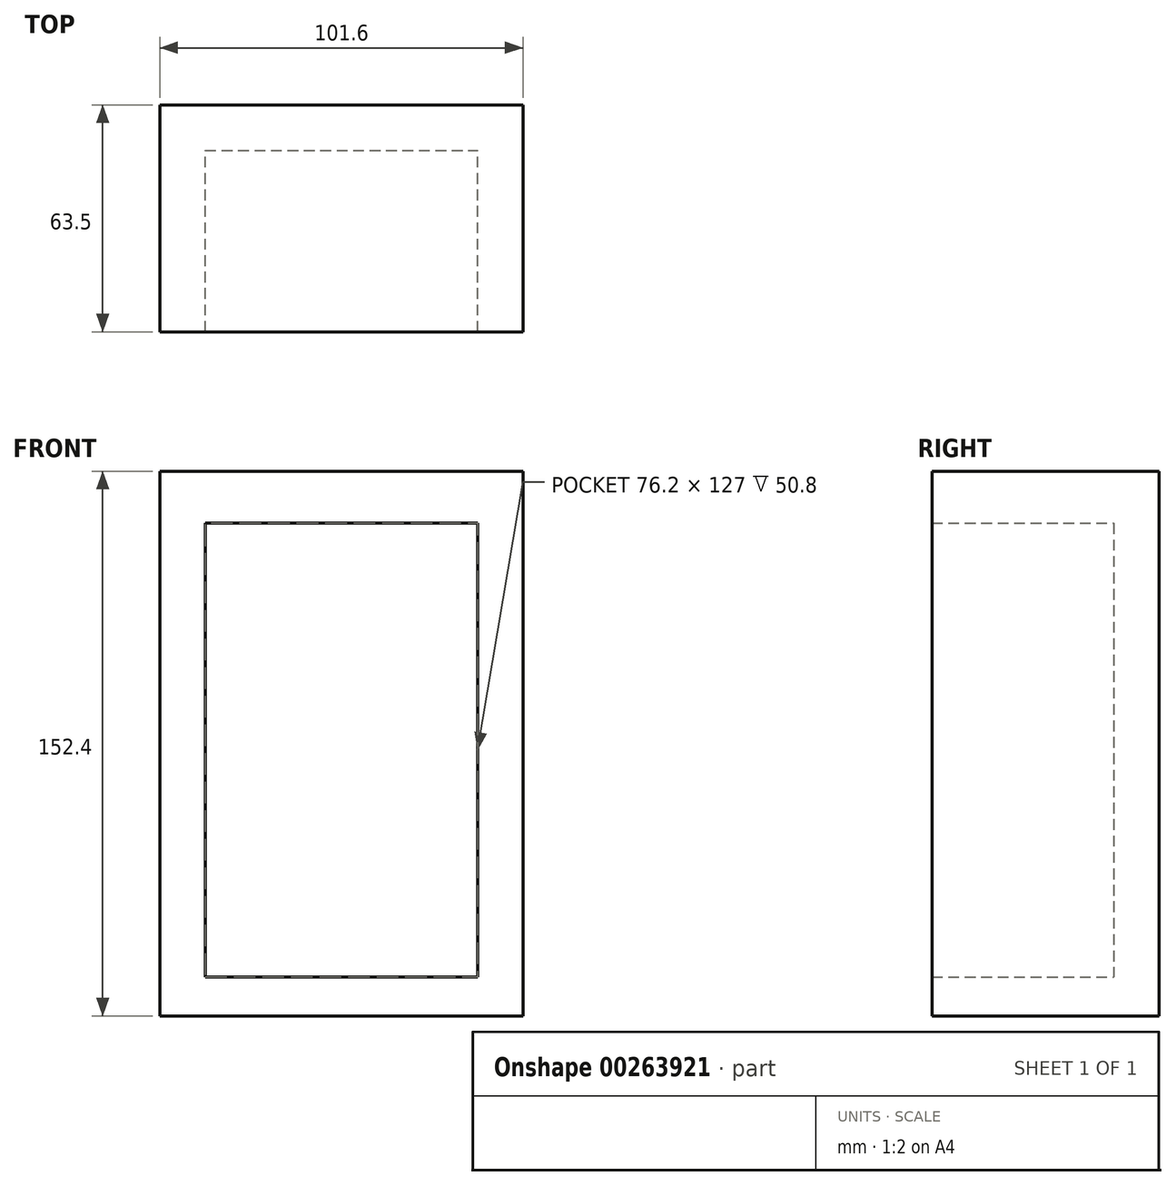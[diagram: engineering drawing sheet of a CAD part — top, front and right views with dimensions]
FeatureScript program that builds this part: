
annotation { "Feature Type Name" : "Feature", "Feature Type Description" : "" }
export const myFeature = defineFeature(function(context is Context, id is Id, definition is map)
    precondition{}
    {
        {
            var Q0;
            Q0=qCreatedBy(makeId("Front.planeOp"),FACE);
            var sketch = newSketch(context, id + "F0", { "sketchPlane" : qUnion([Q0])});
            skLineSegment(sketch, "E0.bottom", {"start": v(-50.8, 76.2) * mm, "end": v(50.8, 76.2) * mm});
            skLineSegment(sketch, "E0.top", {"start": v(-50.8, -76.2) * mm, "end": v(50.8, -76.2) * mm});
            skLineSegment(sketch, "E0.left", {"start": v(-50.8, 76.2) * mm, "end": v(-50.8, -76.2) * mm});
            skLineSegment(sketch, "E0.right", {"start": v(50.8, 76.2) * mm, "end": v(50.8, -76.2) * mm});
            skPoint(sketch, "E0.middle", {"position": v(0, 0) * mm});
            skLineSegment(sketch, "E1.bottom", {"start": v(-38.1, 61.62) * mm, "end": v(38.1, 61.62) * mm});
            skLineSegment(sketch, "E1.top", {"start": v(-38.1, -65.38) * mm, "end": v(38.1, -65.38) * mm});
            skLineSegment(sketch, "E1.left", {"start": v(-38.1, 61.62) * mm, "end": v(-38.1, -65.38) * mm});
            skLineSegment(sketch, "E1.right", {"start": v(38.1, 61.62) * mm, "end": v(38.1, -65.38) * mm});
            skPoint(sketch, "E1.middle", {"position": v(0, -1.88) * mm});
            skSolve(sketch);
        }
        {
            var Q0;
            Q0=makeQuery(id+"F0.imprint","IMPRINT",FACE,{"disambiguationData":[TD([[makeQuery(id+"F0.imprint","IMPRINT",EDGE,{"derivedFrom":sQuery(id+"F0.wireOp",EDGE,"E0.bottom")}),-1.0]])]});
            extrude(context, id + "F1", {"entities" : qUnion([Q0]), "depth" : 63.5 * mm});
        }
        {
            var Q0;
            Q0=makeQuery(id+"F0.imprint","IMPRINT",FACE,{"disambiguationData":[TD([[makeQuery(id+"F0.imprint","IMPRINT",EDGE,{"derivedFrom":sQuery(id+"F0.wireOp",EDGE,"E1.bottom")}),-1.0]])]});
            extrude(context, id + "F2", {"entities" : qUnion([Q0]), "operationType" : NewBodyOperationType.ADD, "depth" : 12.7 * mm});
        }
    });
